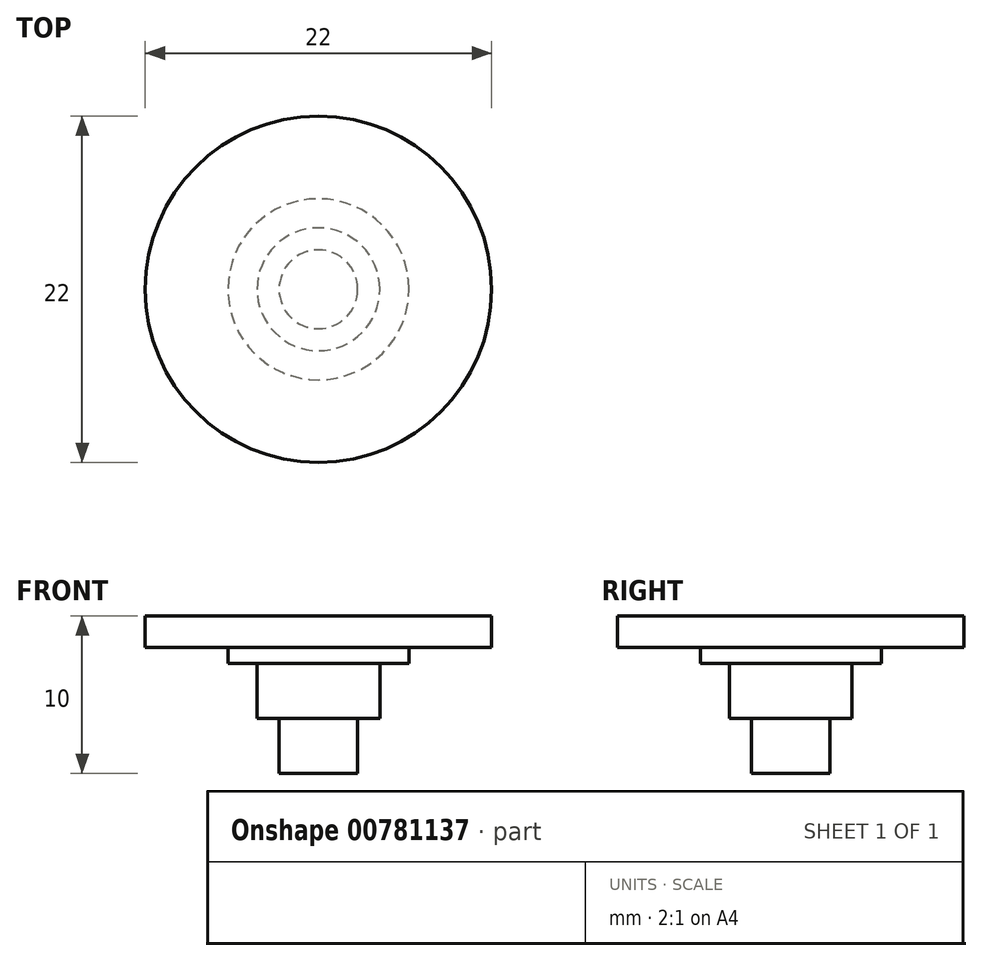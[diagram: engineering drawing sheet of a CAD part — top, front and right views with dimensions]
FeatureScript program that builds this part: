
annotation { "Feature Type Name" : "Feature", "Feature Type Description" : "" }
export const myFeature = defineFeature(function(context is Context, id is Id, definition is map)
    precondition{}
    {
        {
            var Q0;
            Q0=qCreatedBy(makeId("Top.planeOp"),FACE);
            var sketch = newSketch(context, id + "F0", { "sketchPlane" : qUnion([Q0])});
            skCircle(sketch, "E0", {"center": v(0, 0) * mm, "radius": 11 * mm});
            skSolve(sketch);
        }
        {
            var Q0;
            Q0=makeQuery(id+"F0.imprint","IMPRINT",FACE,{"disambiguationData":[TD([[makeQuery(id+"F0.imprint","IMPRINT",EDGE,{"derivedFrom":sQuery(id+"F0.wireOp",EDGE,"E0")}),1.0]])]});
            extrude(context, id + "F1", {"entities" : qUnion([Q0]), "depth" : 6.5 * mm, "offsetDistance" : 25 * mm, "hasSecondDirection" : true, "secondDirectionOppositeDirection" : false, "secondDirectionDepth" : 4.5 * mm});
        }
        {
            var Q0;
            Q0=qCreatedBy(makeId("Top.planeOp"),FACE);
            var sketch = newSketch(context, id + "F2", { "sketchPlane" : qUnion([Q0])});
            skCircle(sketch, "E1", {"center": v(0, 0) * mm, "radius": 3.9 * mm});
            skSolve(sketch);
        }
        {
            var Q0;
            Q0=makeQuery(id+"F2.imprint","IMPRINT",FACE,{"disambiguationData":[TD([[makeQuery(id+"F2.imprint","IMPRINT",EDGE,{"derivedFrom":sQuery(id+"F2.wireOp",EDGE,"E1")}),1.0]])]});
            extrude(context, id + "F3", {"entities" : qUnion([Q0]), "operationType" : NewBodyOperationType.ADD, "depth" : 3.5 * mm, "offsetDistance" : 25 * mm});
        }
        {
            var Q0;
            Q0=qCreatedBy(makeId("Top.planeOp"),FACE);
            var sketch = newSketch(context, id + "F4", { "sketchPlane" : qUnion([Q0])});
            skCircle(sketch, "E2", {"center": v(0, 0) * mm, "radius": 2.5 * mm});
            skSolve(sketch);
        }
        {
            var Q0;
            Q0=makeQuery(id+"F4.imprint","IMPRINT",FACE,{"disambiguationData":[TD([[makeQuery(id+"F4.imprint","IMPRINT",EDGE,{"derivedFrom":sQuery(id+"F4.wireOp",EDGE,"E2")}),1.0]])]});
            extrude(context, id + "F5", {"entities" : qUnion([Q0]), "depth" : 0 * mm, "offsetDistance" : 25 * mm, "hasSecondDirection" : true, "secondDirectionOppositeDirection" : true, "secondDirectionDepth" : 3.5 * mm});
        }
        {
            var Q0;
            Q0=qCreatedBy(makeId("Top.planeOp"),FACE);
            var sketch = newSketch(context, id + "F6", { "sketchPlane" : qUnion([Q0])});
            skCircle(sketch, "E3", {"center": v(0, 0) * mm, "radius": 5.75 * mm});
            skSolve(sketch);
        }
        {
            var Q0;
            Q0=makeQuery(id+"F6.imprint","IMPRINT",FACE,{"disambiguationData":[TD([[makeQuery(id+"F6.imprint","IMPRINT",EDGE,{"derivedFrom":sQuery(id+"F6.wireOp",EDGE,"E3")}),1.0]])]});
            extrude(context, id + "F7", {"entities" : qUnion([Q0]), "depth" : 4.5 * mm, "offsetDistance" : 25 * mm, "hasSecondDirection" : true, "secondDirectionOppositeDirection" : false, "secondDirectionDepth" : 3.5 * mm});
        }
    });
